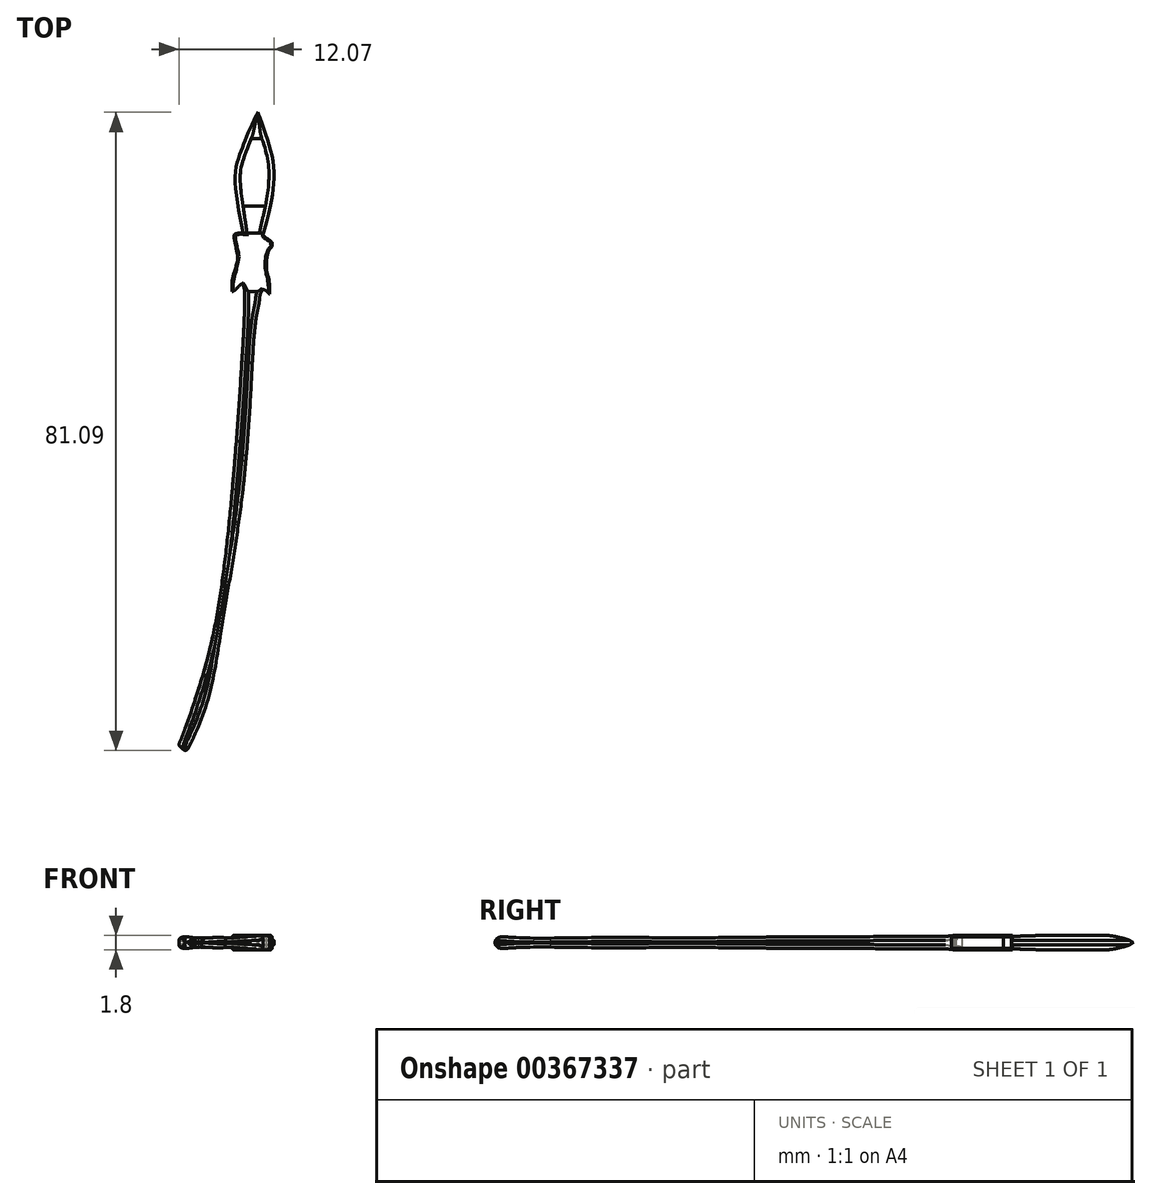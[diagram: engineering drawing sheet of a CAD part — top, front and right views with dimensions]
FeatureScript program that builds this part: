
annotation { "Feature Type Name" : "Feature", "Feature Type Description" : "" }
export const myFeature = defineFeature(function(context is Context, id is Id, definition is map)
    precondition{}
    {
        {
            var Q0;
            Q0=qCreatedBy(makeId("Top.planeOp"),FACE);
            var sketch = newSketch(context, id + "F0", { "sketchPlane" : qUnion([Q0])});
            skLineSegment(sketch, "E0", {"start": v(0, 0) * mm, "end": v(0, 81.53) * mm, "construction": true});
            skLineSegment(sketch, "E1", {"start": v(0, 0) * mm, "end": v(-71.64, 0) * mm, "construction": true});
            skLineSegment(sketch, "E2", {"start": v(-71.64, 0) * mm, "end": v(-71.64, 6.26) * mm, "construction": true});
            skLineSegment(sketch, "E3", {"start": v(0, 81.53) * mm, "end": v(-62.4, 81.53) * mm, "construction": true});
            skLineSegment(sketch, "E4", {"start": v(-62.4, 81.53) * mm, "end": v(-62.4, 87.8) * mm, "construction": true});
            skPoint(sketch, "E5", {"position": v(-64.3, 72.44) * mm});
            skPoint(sketch, "E6", {"position": v(-65.38, 72.3) * mm});
            skPoint(sketch, "E7", {"position": v(-60.62, 71.27) * mm});
            skPoint(sketch, "E8", {"position": v(-60.9, 64.67) * mm});
            skPoint(sketch, "E9", {"position": v(-61.73, 65.26) * mm});
            skPoint(sketch, "E10", {"position": v(-64.38, 66.03) * mm});
            skPoint(sketch, "E11", {"position": v(-65.65, 65) * mm});
            skPoint(sketch, "E12", {"position": v(-61.73, 72.33) * mm});
            skPoint(sketch, "E13", {"position": v(-71.34, 6.78) * mm});
            skPoint(sketch, "E14", {"position": v(-72.38, 7.59) * mm});
            skFitSpline(sketch, "E15", {"points": [v(-62.4, 87.8) * mm, v(-63.77, 84.82) * mm, v(-64.59, 82.67) * mm, v(-65.27, 79.88) * mm, v(-64.3, 72.44) * mm], "startDerivative": vector(-6.4, -13.24) * mm, "endDerivative": vector(4.62, -23.58) * mm});
            skFitSpline(sketch, "E16", {"points": [v(-61.73, 72.33) * mm, v(-60.9, 75.4) * mm, v(-60.41, 81.11) * mm, v(-62.4, 87.8) * mm], "startDerivative": vector(3.3, 11.5) * mm, "endDerivative": vector(-6.87, 20.53) * mm});
            skFitSpline(sketch, "E17", {"points": [v(-64.3, 72.44) * mm, v(-64.64, 72.44) * mm, v(-65, 72.4) * mm, v(-65.38, 72.3) * mm], "startDerivative": vector(-0.76, 0.06) * mm, "endDerivative": vector(-1.51, -0.34) * mm});
            skFitSpline(sketch, "E18", {"points": [v(-65.38, 72.3) * mm, v(-65.38, 71.56) * mm, v(-65.06, 70.17) * mm, v(-64.98, 69.19) * mm, v(-65.38, 67.46) * mm, v(-65.64, 66.41) * mm, v(-65.65, 65) * mm], "startDerivative": vector(-0.44, -5.18) * mm, "endDerivative": vector(0.35, -8.4) * mm});
            skFitSpline(sketch, "E19", {"points": [v(-65.65, 65) * mm, v(-65.12, 65.39) * mm, v(-64.75, 65.72) * mm, v(-64.38, 66.03) * mm], "startDerivative": vector(1.85, 0.93) * mm, "endDerivative": vector(2, 0.91) * mm});
            skFitSpline(sketch, "E20", {"points": [v(-61.73, 72.33) * mm, v(-61.62, 72.04) * mm, v(-60.85, 71.47) * mm, v(-60.62, 71.27) * mm], "startDerivative": vector(0.13, -1.02) * mm, "endDerivative": vector(0.63, -0.65) * mm});
            skFitSpline(sketch, "E21", {"points": [v(-60.62, 71.27) * mm, v(-60.62, 70.72) * mm, v(-61, 70.2) * mm, v(-61.3, 67.99) * mm, v(-60.96, 66.3) * mm, v(-60.9, 64.67) * mm], "startDerivative": vector(0.63, -5.8) * mm, "endDerivative": vector(0.57, -8.34) * mm});
            skFitSpline(sketch, "E22", {"points": [v(-61.73, 65.26) * mm, v(-61.5, 65.2) * mm, v(-61.2, 64.95) * mm, v(-60.9, 64.67) * mm], "startDerivative": vector(1.08, -0.24) * mm, "endDerivative": vector(1.46, -0.58) * mm});
            skFitSpline(sketch, "E23", {"points": [v(-64.38, 66.03) * mm, v(-64.18, 65.62) * mm, v(-64.07, 63.17) * mm, v(-65.56, 40.84) * mm, v(-67.28, 25.8) * mm, v(-68.55, 19.36) * mm, v(-69.9, 14.56) * mm, v(-71.54, 9.76) * mm, v(-72.38, 7.59) * mm], "startDerivative": vector(6.2, -10.35) * mm, "endDerivative": vector(-9.85, -24.6) * mm});
            skFitSpline(sketch, "E24", {"points": [v(-61.73, 65.26) * mm, v(-62.05, 64.77) * mm, v(-62.23, 63.66) * mm, v(-62.67, 61.29) * mm, v(-63.55, 48.07) * mm, v(-65.1, 33.86) * mm, v(-66.63, 24.63) * mm, v(-67.69, 18.06) * mm, v(-68.46, 14.21) * mm, v(-69.52, 10.9) * mm, v(-71.34, 6.78) * mm], "startDerivative": vector(-8.91, -12.12) * mm, "endDerivative": vector(-21.42, -42.54) * mm});
            skFitSpline(sketch, "E25", {"points": [v(-72.38, 7.59) * mm, v(-72.42, 7.5) * mm, v(-72.38, 7.33) * mm, v(-71.66, 6.71) * mm, v(-71.39, 6.72) * mm, v(-71.34, 6.78) * mm], "startDerivative": vector(-0.35, -0.93) * mm, "endDerivative": vector(0.3, 0.53) * mm});
            skSolve(sketch);
        }
        {
            var Q0;
            Q0=makeQuery(id+"F0.imprint","IMPRINT",FACE,{"disambiguationData":[TD([[makeQuery(id+"F0.imprint","IMPRINT",EDGE,{"derivedFrom":sQuery(id+"F0.wireOp",EDGE,"E15")}),1.0]])]});
            extrude(context, id + "F1", {"entities" : qUnion([Q0]), "depth" : 1.8 * mm});
        }
        {
            var Q0;
            Q0=qCreatedBy(makeId("Right.planeOp"),FACE);
            var sketch = newSketch(context, id + "F2", { "sketchPlane" : qUnion([Q0])});
            skFitSpline(sketch, "E26.0", {"points": [v(87.8, 0) * mm, v(86.76, 0) * mm, v(84.87, 0) * mm, v(82.62, 0) * mm, v(79.71, 0) * mm, v(75.21, 0) * mm, v(72.44, 0) * mm], "construction": true});
            skLineSegment(sketch, "E27", {"start": v(72.44, 1.8) * mm, "end": v(72.44, 0) * mm, "construction": true});
            skFitSpline(sketch, "E28.0.0", {"points": [v(72.3, 0) * mm, v(72.08, 0) * mm, v(71.55, 0) * mm, v(70.13, 0) * mm, v(69.21, 0) * mm, v(67.42, 0) * mm, v(66.44, 0) * mm, v(65.5, 0) * mm, v(65, 0) * mm], "construction": true});
            skLineSegment(sketch, "E28.0.1", {"start": v(65, 0) * mm, "end": v(65, 1.8) * mm, "construction": true});
            skFitSpline(sketch, "E28.0.2", {"points": [v(65, 1.8) * mm, v(65.5, 1.8) * mm, v(66.44, 1.8) * mm, v(67.42, 1.8) * mm, v(69.21, 1.8) * mm, v(70.13, 1.8) * mm, v(71.55, 1.8) * mm, v(72.08, 1.8) * mm, v(72.3, 1.8) * mm], "construction": true});
            skLineSegment(sketch, "E28.0.3", {"start": v(72.3, 1.8) * mm, "end": v(72.3, 0) * mm, "construction": true});
            skFitSpline(sketch, "E29.0.0", {"points": [v(66.03, 0) * mm, v(65.91, 0) * mm, v(65.52, 0) * mm, v(62.47, 0) * mm, v(40.2, 0) * mm, v(26.43, 0) * mm, v(19.45, 0) * mm, v(14.7, 0) * mm, v(9.82, 0) * mm, v(8.23, 0) * mm, v(7.59, 0) * mm], "construction": true});
            skLineSegment(sketch, "E29.0.1", {"start": v(7.59, 0) * mm, "end": v(7.59, 1.8) * mm, "construction": true});
            skFitSpline(sketch, "E29.0.2", {"points": [v(7.59, 1.8) * mm, v(8.23, 1.8) * mm, v(9.82, 1.8) * mm, v(14.7, 1.8) * mm, v(19.45, 1.8) * mm, v(26.43, 1.8) * mm, v(40.2, 1.8) * mm, v(62.47, 1.8) * mm, v(65.52, 1.8) * mm, v(65.91, 1.8) * mm, v(66.03, 1.8) * mm], "construction": true});
            skLineSegment(sketch, "E29.0.3", {"start": v(66.03, 1.8) * mm, "end": v(66.03, 0) * mm, "construction": true});
            skPoint(sketch, "E30.0", {"position": v(6.78, 0) * mm});
            skPoint(sketch, "E31.0", {"position": v(6.95, 0) * mm});
            skLineSegment(sketch, "E32", {"start": v(6.69, 0) * mm, "end": v(6.69, 1.8) * mm, "construction": true});
            skLineSegment(sketch, "E33.0", {"start": v(87.8, 1.8) * mm, "end": v(87.8, 0) * mm, "construction": true});
            skFitSpline(sketch, "E34.0.0", {"points": [v(87.8, 0) * mm, v(86.76, 0) * mm, v(84.87, 0) * mm, v(82.62, 0) * mm, v(79.71, 0) * mm, v(75.21, 0) * mm, v(72.44, 0) * mm], "construction": true});
            skLineSegment(sketch, "E34.0.1", {"start": v(72.44, 0) * mm, "end": v(72.44, 1.8) * mm, "construction": true});
            skFitSpline(sketch, "E34.0.2", {"points": [v(72.44, 1.8) * mm, v(75.21, 1.8) * mm, v(79.71, 1.8) * mm, v(82.62, 1.8) * mm, v(84.87, 1.8) * mm, v(86.76, 1.8) * mm, v(87.8, 1.8) * mm], "construction": true});
            skLineSegment(sketch, "E35", {"start": v(87.8, 0.9) * mm, "end": v(6.69, 0.9) * mm, "construction": true});
            skLineSegment(sketch, "E36", {"start": v(87.13, 0.9) * mm, "end": v(87.13, 1.26) * mm, "construction": true});
            skLineSegment(sketch, "E37", {"start": v(85.68, 0.9) * mm, "end": v(85.68, 1.64) * mm});
            skPoint(sketch, "E38", {"position": v(84.46, 1.8) * mm});
            skPoint(sketch, "E39", {"position": v(75.9, 1.8) * mm});
            skPoint(sketch, "E40", {"position": v(72.44, 1.67) * mm});
            skPoint(sketch, "E41", {"position": v(72.44, 1.8) * mm});
            skLineSegment(sketch, "E42", {"start": v(63.98, 0.9) * mm, "end": v(63.98, 1.7) * mm});
            skLineSegment(sketch, "E43", {"start": v(61.65, 0.9) * mm, "end": v(61.65, 1.69) * mm});
            skLineSegment(sketch, "E44", {"start": v(54.8, 0.9) * mm, "end": v(54.8, 1.66) * mm});
            skLineSegment(sketch, "E45", {"start": v(44.68, 0.9) * mm, "end": v(44.68, 1.61) * mm});
            skLineSegment(sketch, "E46", {"start": v(39.4, 0.9) * mm, "end": v(39.4, 1.59) * mm});
            skLineSegment(sketch, "E47", {"start": v(30.16, 0.9) * mm, "end": v(30.16, 1.51) * mm});
            skLineSegment(sketch, "E48", {"start": v(21.2, 0.9) * mm, "end": v(21.2, 1.56) * mm});
            skLineSegment(sketch, "E49", {"start": v(9.38, 0.9) * mm, "end": v(9.38, 1.54) * mm});
            skFitSpline(sketch, "E50", {"points": [v(6.69, 0.9) * mm, v(7.04, 1.5) * mm, v(9.38, 1.54) * mm, v(21.2, 1.56) * mm, v(30.16, 1.51) * mm, v(39.4, 1.59) * mm, v(44.68, 1.61) * mm, v(54.8, 1.66) * mm, v(61.65, 1.69) * mm, v(63.98, 1.7) * mm, v(65, 1.8) * mm], "startDerivative": vector(6.44, 18.9) * mm, "endDerivative": vector(20.96, 2.7) * mm});
            skLineSegment(sketch, "E51", {"start": v(65, 1.8) * mm, "end": v(72.44, 1.8) * mm});
            skLineSegment(sketch, "E52", {"start": v(72.44, 1.8) * mm, "end": v(72.44, 1.67) * mm});
            skFitSpline(sketch, "E53", {"points": [v(72.44, 1.67) * mm, v(73.74, 1.74) * mm, v(75.9, 1.8) * mm], "startDerivative": vector(2.78, 0.19) * mm, "endDerivative": vector(4.07, 0.09) * mm});
            skLineSegment(sketch, "E54", {"start": v(75.9, 1.8) * mm, "end": v(84.46, 1.8) * mm});
            skFitSpline(sketch, "E55", {"points": [v(84.46, 1.8) * mm, v(85.02, 1.77) * mm, v(85.68, 1.64) * mm, v(87.13, 1.26) * mm, v(87.8, 0.9) * mm], "startDerivative": vector(2.78, -0.08) * mm, "endDerivative": vector(2.35, -1.55) * mm});
            skLineSegment(sketch, "E56", {"start": v(88.45, 1.86) * mm, "end": v(87.45, 2.77) * mm});
            skLineSegment(sketch, "E57", {"start": v(87.45, 2.77) * mm, "end": v(6.36, 2.4) * mm});
            skLineSegment(sketch, "E58", {"start": v(6.36, 2.4) * mm, "end": v(6.52, 0.9) * mm});
            skLineSegment(sketch, "E59.MirrorCS", {"start": v(72.44, 0) * mm, "end": v(72.44, 0.14) * mm});
            skLineSegment(sketch, "E60.MirrorCS", {"start": v(6.69, 1.8) * mm, "end": v(6.69, 0) * mm, "construction": true});
            skLineSegment(sketch, "E61.MirrorCS", {"start": v(87.8, 0) * mm, "end": v(87.8, 1.8) * mm, "construction": true});
            skLineSegment(sketch, "E62.MirrorCS", {"start": v(72.3, 0) * mm, "end": v(72.3, 1.8) * mm, "construction": true});
            skLineSegment(sketch, "E63.MirrorCS", {"start": v(87.13, 0.9) * mm, "end": v(87.13, 0.55) * mm, "construction": true});
            skLineSegment(sketch, "E64.MirrorCS", {"start": v(6.36, -0.59) * mm, "end": v(6.52, 0.9) * mm});
            skLineSegment(sketch, "E65.MirrorCS", {"start": v(63.98, 0.9) * mm, "end": v(63.98, 0.1) * mm});
            skLineSegment(sketch, "E66.MirrorCS", {"start": v(44.68, 0.9) * mm, "end": v(44.68, 0.2) * mm});
            skLineSegment(sketch, "E67.MirrorCS", {"start": v(9.38, 0.9) * mm, "end": v(9.38, 0.27) * mm});
            skLineSegment(sketch, "E68.MirrorCS", {"start": v(21.2, 0.9) * mm, "end": v(21.2, 0.24) * mm});
            skLineSegment(sketch, "E69.MirrorCS", {"start": v(85.68, 0.9) * mm, "end": v(85.68, 0.17) * mm});
            skLineSegment(sketch, "E70.MirrorCS", {"start": v(30.16, 0.9) * mm, "end": v(30.16, 0.3) * mm});
            skLineSegment(sketch, "E71.MirrorCS", {"start": v(54.8, 0.9) * mm, "end": v(54.8, 0.14) * mm});
            skFitSpline(sketch, "E72.MirrorCS", {"points": [v(84.46, 0) * mm, v(85.02, 0.03) * mm, v(85.68, 0.17) * mm, v(87.13, 0.55) * mm, v(87.8, 0.9) * mm], "startDerivative": vector(2.78, 0.08) * mm, "endDerivative": vector(2.35, 1.55) * mm});
            skLineSegment(sketch, "E73.MirrorCS", {"start": v(88.45, -0.06) * mm, "end": v(87.45, -0.97) * mm});
            skLineSegment(sketch, "E74.MirrorCS", {"start": v(65, 1.8) * mm, "end": v(65, 0) * mm, "construction": true});
            skLineSegment(sketch, "E75.MirrorCS", {"start": v(39.4, 0.9) * mm, "end": v(39.4, 0.22) * mm});
            skLineSegment(sketch, "E76.MirrorCS", {"start": v(61.65, 0.9) * mm, "end": v(61.65, 0.11) * mm});
            skLineSegment(sketch, "E77.MirrorCS", {"start": v(7.59, 1.8) * mm, "end": v(7.59, 0) * mm, "construction": true});
            skLineSegment(sketch, "E78.MirrorCS", {"start": v(66.03, 0) * mm, "end": v(66.03, 1.8) * mm, "construction": true});
            skFitSpline(sketch, "E79.MirrorCS", {"points": [v(72.44, 0.14) * mm, v(73.74, 0.06) * mm, v(75.9, 0) * mm], "startDerivative": vector(2.78, -0.19) * mm, "endDerivative": vector(4.07, -0.09) * mm});
            skLineSegment(sketch, "E80.MirrorCS", {"start": v(65, 0) * mm, "end": v(72.44, 0) * mm});
            skPoint(sketch, "E81.MirrorP", {"position": v(6.78, 1.8) * mm});
            skFitSpline(sketch, "E82.MirrorCS", {"points": [v(87.8, 1.8) * mm, v(86.76, 1.8) * mm, v(84.87, 1.8) * mm, v(82.62, 1.8) * mm, v(79.71, 1.8) * mm, v(75.21, 1.8) * mm, v(72.44, 1.8) * mm], "construction": true});
            skLineSegment(sketch, "E83.MirrorCS", {"start": v(75.9, 0) * mm, "end": v(84.46, 0) * mm});
            skLineSegment(sketch, "E84.MirrorCS", {"start": v(87.45, -0.97) * mm, "end": v(6.36, -0.59) * mm});
            skFitSpline(sketch, "E85.MirrorCS", {"points": [v(6.69, 0.9) * mm, v(7.04, 0.3) * mm, v(9.38, 0.27) * mm, v(21.2, 0.24) * mm, v(30.16, 0.3) * mm, v(39.4, 0.22) * mm, v(44.68, 0.2) * mm, v(54.8, 0.14) * mm, v(61.65, 0.11) * mm, v(63.98, 0.1) * mm, v(65, 0) * mm], "startDerivative": vector(6.44, -18.9) * mm, "endDerivative": vector(20.96, -2.7) * mm});
            skFitSpline(sketch, "E86.MirrorCS", {"points": [v(72.3, 1.8) * mm, v(72.08, 1.8) * mm, v(71.55, 1.8) * mm, v(70.13, 1.8) * mm, v(69.21, 1.8) * mm, v(67.42, 1.8) * mm, v(66.44, 1.8) * mm, v(65.5, 1.8) * mm, v(65, 1.8) * mm], "construction": true});
            skFitSpline(sketch, "E87.MirrorCS", {"points": [v(72.44, 0) * mm, v(75.21, 0) * mm, v(79.71, 0) * mm, v(82.62, 0) * mm, v(84.87, 0) * mm, v(86.76, 0) * mm, v(87.8, 0) * mm], "construction": true});
            skFitSpline(sketch, "E88.MirrorCS", {"points": [v(65, 0) * mm, v(65.5, 0) * mm, v(66.44, 0) * mm, v(67.42, 0) * mm, v(69.21, 0) * mm, v(70.13, 0) * mm, v(71.55, 0) * mm, v(72.08, 0) * mm, v(72.3, 0) * mm], "construction": true});
            skFitSpline(sketch, "E89.MirrorCS", {"points": [v(66.03, 1.8) * mm, v(65.91, 1.8) * mm, v(65.52, 1.8) * mm, v(62.47, 1.8) * mm, v(40.2, 1.8) * mm, v(26.43, 1.8) * mm, v(19.45, 1.8) * mm, v(14.7, 1.8) * mm, v(9.82, 1.8) * mm, v(8.23, 1.8) * mm, v(7.59, 1.8) * mm], "construction": true});
            skPoint(sketch, "E90.MirrorP", {"position": v(72.44, 0) * mm});
            skFitSpline(sketch, "E91.MirrorCS", {"points": [v(87.8, 1.8) * mm, v(86.76, 1.8) * mm, v(84.87, 1.8) * mm, v(82.62, 1.8) * mm, v(79.71, 1.8) * mm, v(75.21, 1.8) * mm, v(72.44, 1.8) * mm], "construction": true});
            skFitSpline(sketch, "E92.MirrorCS", {"points": [v(7.59, 0) * mm, v(8.23, 0) * mm, v(9.82, 0) * mm, v(14.7, 0) * mm, v(19.45, 0) * mm, v(26.43, 0) * mm, v(40.2, 0) * mm, v(62.47, 0) * mm, v(65.52, 0) * mm, v(65.91, 0) * mm, v(66.03, 0) * mm], "construction": true});
            skPoint(sketch, "E93.MirrorP", {"position": v(6.95, 1.8) * mm});
            skLineSegment(sketch, "E94", {"start": v(88.45, 1.86) * mm, "end": v(88.45, -0.06) * mm});
            skSolve(sketch);
        }
        {
            var Q0;
            Q0=makeQuery(id+"F2.imprint","IMPRINT",FACE,{"disambiguationData":[TD([[makeQuery(id+"F2.imprint","IMPRINT",EDGE,{"derivedFrom":sQuery(id+"F2.wireOp",EDGE,"E59.MirrorCS")}),-1.0]])]});
            var Q1;
            {var subQ0=sQuery(id+"F2.wireOp",EDGE,"E51");Q1=makeQuery(id+"F2.imprint","IMPRINT",FACE,{"disambiguationData":[TD([[makeQuery(id+"F2.imprint","IMPRINT",EDGE,{"derivedFrom":subQ0}),1.0]])]});}
            extrude(context, id + "F3", {"entities" : qUnion([Q0, Q1]), "operationType" : NewBodyOperationType.REMOVE, "endBound" : BoundingType.THROUGH_ALL, "oppositeDirection" : true, "depth" : 25.4 * mm});
        }
        {
            var Q0;
            Q0=makeQuery(id+"F1.opExtrude","CAP_EDGE",EDGE,{"disambiguationData":[OSD([sQuery(id+"F0.wireOp",EDGE,"E15")])],"isStart":false});
            var Q1;
            {var subQ0=sQuery(id+"F0.wireOp",EDGE,"E16");Q1=makeQuery(id+"F3.boolean.opBoolean","SPLIT",EDGE,{"disambiguationData":[TD([makeQuery(id+"F3.opExtrude","SWEPT_FACE",FACE,{"disambiguationData":[OSD([sQuery(id+"F2.wireOp",EDGE,"E53")])]})])],"derivedFrom":makeQuery(id+"F1.opExtrude","CAP_EDGE",EDGE,{"disambiguationData":[OSD([subQ0])],"isStart":false})});}
            var Q2;
            Q2=makeQuery(id+"F1.opExtrude","CAP_EDGE",EDGE,{"disambiguationData":[OSD([sQuery(id+"F0.wireOp",EDGE,"E15")])],"isStart":true});
            var Q3;
            {var subQ0=sQuery(id+"F0.wireOp",EDGE,"E16");Q3=makeQuery(id+"F3.boolean.opBoolean","SPLIT",EDGE,{"disambiguationData":[TD([makeQuery(id+"F3.opExtrude","SWEPT_FACE",FACE,{"disambiguationData":[OSD([sQuery(id+"F2.wireOp",EDGE,"E72.MirrorCS")])]})])],"derivedFrom":makeQuery(id+"F1.opExtrude","CAP_EDGE",EDGE,{"disambiguationData":[OSD([subQ0])],"isStart":true})});}
            chamfer(context, id + "F4", {"entities" : qUnion([Q0, Q1, Q2, Q3]), "width" : 0.64 * mm, "tangentPropagation" : true});
        }
        {
            var Q0;
            Q0=makeQuery(id+"F1.opExtrude","CAP_EDGE",EDGE,{"disambiguationData":[OSD([sQuery(id+"F0.wireOp",EDGE,"E21")])],"isStart":false});
            var Q1;
            Q1=makeQuery(id+"F1.opExtrude","CAP_EDGE",EDGE,{"disambiguationData":[OSD([sQuery(id+"F0.wireOp",EDGE,"E18")])],"isStart":false});
            var Q2;
            Q2=makeQuery(id+"F1.opExtrude","CAP_EDGE",EDGE,{"disambiguationData":[OSD([sQuery(id+"F0.wireOp",EDGE,"E21")])],"isStart":true});
            var Q3;
            Q3=makeQuery(id+"F1.opExtrude","CAP_EDGE",EDGE,{"disambiguationData":[OSD([sQuery(id+"F0.wireOp",EDGE,"E20")])],"isStart":false});
            var Q4;
            Q4=makeQuery(id+"F3.boolean.opBoolean","SPLIT",EDGE,{"derivedFrom":makeQuery(id+"F1.opExtrude","CAP_EDGE",EDGE,{"disambiguationData":[OSD([sQuery(id+"F0.wireOp",EDGE,"E17")])],"isStart":false})});
            var Q5;
            Q5=makeQuery(id+"F1.opExtrude","CAP_EDGE",EDGE,{"disambiguationData":[OSD([sQuery(id+"F0.wireOp",EDGE,"E20")])],"isStart":true});
            var Q6;
            Q6=makeQuery(id+"F3.boolean.opBoolean","SPLIT",EDGE,{"derivedFrom":makeQuery(id+"F1.opExtrude","CAP_EDGE",EDGE,{"disambiguationData":[OSD([sQuery(id+"F0.wireOp",EDGE,"E17")])],"isStart":true})});
            var Q7;
            Q7=makeQuery(id+"F1.opExtrude","CAP_EDGE",EDGE,{"disambiguationData":[OSD([sQuery(id+"F0.wireOp",EDGE,"E18")])],"isStart":true});
            chamfer(context, id + "F5", {"entities" : qUnion([Q0, Q1, Q2, Q3, Q4, Q5, Q6, Q7]), "width" : 0.15 * mm, "tangentPropagation" : true});
        }
        {
            var Q0;
            Q0=makeQuery(id+"F3.boolean.opBoolean","INTERSECT",EDGE,{"derivedFrom":[makeQuery(id+"F1.opExtrude","SWEPT_FACE",FACE,{"disambiguationData":[OSD([sQuery(id+"F0.wireOp",EDGE,"E24")])]}),makeQuery(id+"F3.opExtrude","SWEPT_FACE",FACE,{"disambiguationData":[OSD([sQuery(id+"F2.wireOp",EDGE,"E85.MirrorCS")])]})]});
            var Q1;
            Q1=makeQuery(id+"F3.boolean.opBoolean","INTERSECT",EDGE,{"derivedFrom":[makeQuery(id+"F1.opExtrude","SWEPT_FACE",FACE,{"disambiguationData":[OSD([sQuery(id+"F0.wireOp",EDGE,"E23")])]}),makeQuery(id+"F3.opExtrude","SWEPT_FACE",FACE,{"disambiguationData":[OSD([sQuery(id+"F2.wireOp",EDGE,"E85.MirrorCS")])]})]});
            var Q2;
            Q2=makeQuery(id+"F3.boolean.opBoolean","INTERSECT",EDGE,{"derivedFrom":[makeQuery(id+"F1.opExtrude","SWEPT_FACE",FACE,{"disambiguationData":[OSD([sQuery(id+"F0.wireOp",EDGE,"E24")])]}),makeQuery(id+"F3.opExtrude","SWEPT_FACE",FACE,{"disambiguationData":[OSD([sQuery(id+"F2.wireOp",EDGE,"E50")])]})]});
            var Q3;
            Q3=makeQuery(id+"F3.boolean.opBoolean","INTERSECT",EDGE,{"derivedFrom":[makeQuery(id+"F1.opExtrude","SWEPT_FACE",FACE,{"disambiguationData":[OSD([sQuery(id+"F0.wireOp",EDGE,"E23")])]}),makeQuery(id+"F3.opExtrude","SWEPT_FACE",FACE,{"disambiguationData":[OSD([sQuery(id+"F2.wireOp",EDGE,"E50")])]})]});
            fillet(context, id + "F6", {"entities" : qUnion([Q0, Q1, Q2, Q3]), "radius" : 0.5 * mm, "tangentPropagation" : true, "allowEdgeOverflow" : false});
        }
    });
